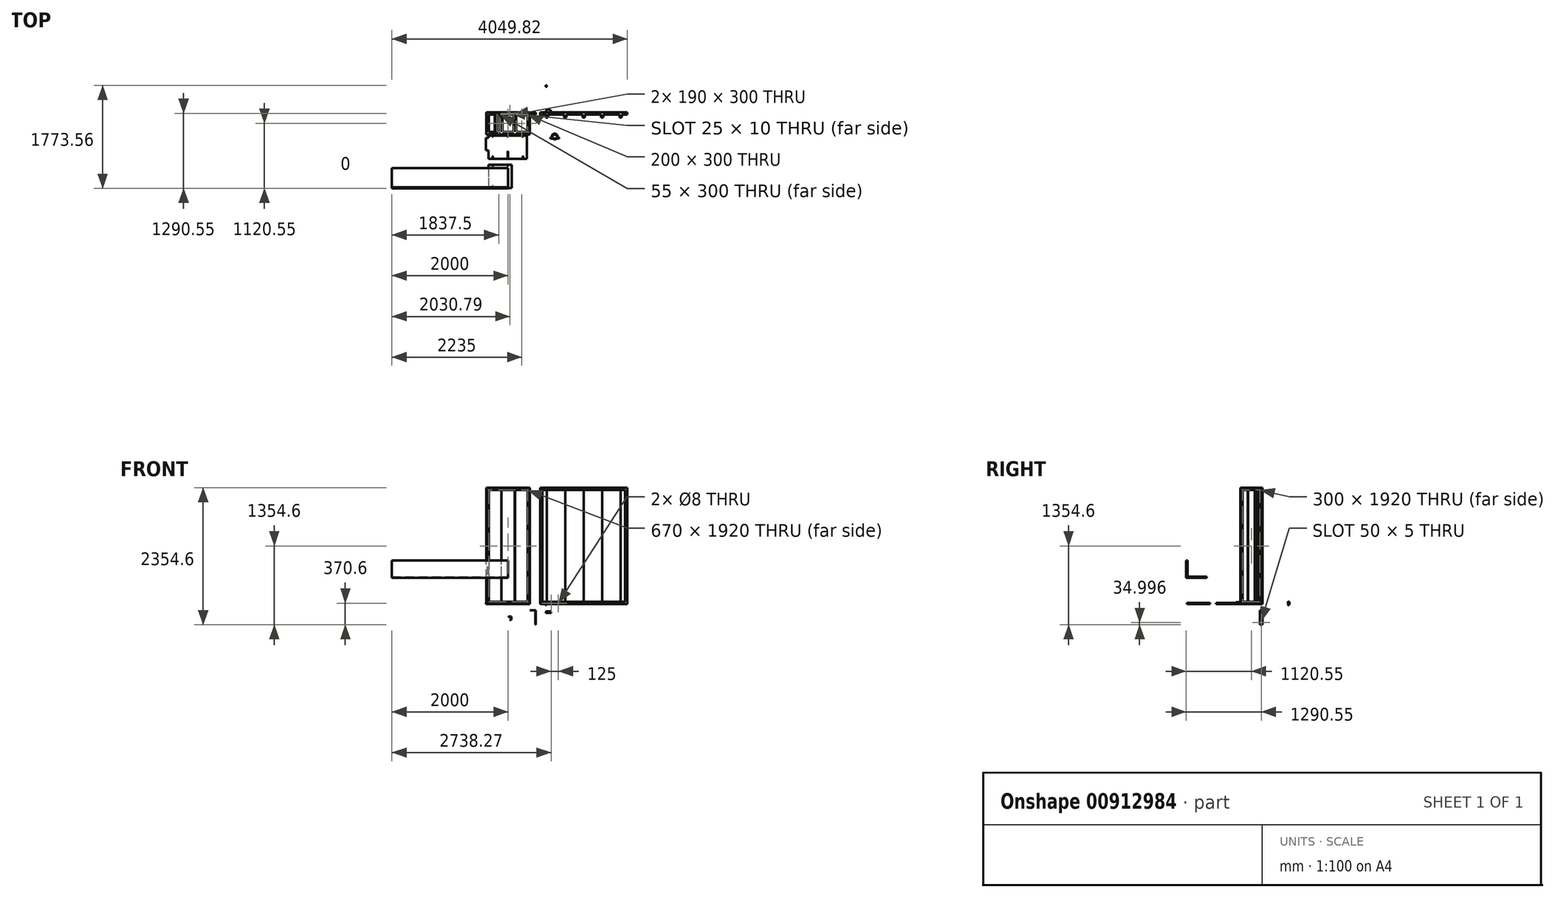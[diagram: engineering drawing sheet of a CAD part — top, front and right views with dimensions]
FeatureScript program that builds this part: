
annotation { "Feature Type Name" : "Feature", "Feature Type Description" : "" }
export const myFeature = defineFeature(function(context is Context, id is Id, definition is map)
    precondition{}
    {
        {
            assignVariable(context, id + "F0", {"name" : "widthA", "anyValue" : 380});
        }
        {
            assignVariable(context, id + "F1", {"name" : "widthB", "anyValue" : 90});
        }
        {
            var Q0;
            Q0=qCreatedBy(makeId("Front.planeOp"),FACE);
            var sketch = newSketch(context, id + "F2", { "sketchPlane" : qUnion([Q0])});
            skLineSegment(sketch, "E0.bottom", {"start": v(0, 0) * mm, "end": v(-750, 0) * mm});
            skLineSegment(sketch, "E0.top", {"start": v(0, 2000) * mm, "end": v(-750, 2000) * mm});
            skLineSegment(sketch, "E0.left", {"start": v(0, 0) * mm, "end": v(0, 2000) * mm});
            skLineSegment(sketch, "E0.right", {"start": v(-750, 0) * mm, "end": v(-750, 2000) * mm});
            skSolve(sketch);
        }
        {
            var Q0;
            Q0 = qSketchRegion(id + "F2", true);
            extrude(context, id + "F3", {"entities" : qUnion([Q0]), "depth" : (getVariable(context, 'widthA')) * mm, "offsetDistance" : 25 * mm});
        }
        {
            var Q0;
            Q0=makeQuery(id+"F3.opExtrude","CAP_FACE",FACE,{"disambiguationData":[OSD([sQuery(id+"F2.wireOp",EDGE,"E0.bottom"),sQuery(id+"F2.wireOp",EDGE,"E0.top"),sQuery(id+"F2.wireOp",EDGE,"E0.left"),sQuery(id+"F2.wireOp",EDGE,"E0.right")])],"isStart":false});
            var sketch = newSketch(context, id + "F4", { "sketchPlane" : qUnion([Q0])});
            skLineSegment(sketch, "E1.bottom", {"start": v(-710, 1960) * mm, "end": v(-40, 1960) * mm});
            skLineSegment(sketch, "E1.top", {"start": v(-710, 40) * mm, "end": v(-40, 40) * mm});
            skLineSegment(sketch, "E1.left", {"start": v(-710, 1960) * mm, "end": v(-710, 40) * mm});
            skLineSegment(sketch, "E1.right", {"start": v(-40, 1960) * mm, "end": v(-40, 40) * mm});
            skSolve(sketch);
        }
        {
            var Q0;
            Q0 = qSketchRegion(id + "F4", true);
            extrude(context, id + "F5", {"entities" : qUnion([Q0]), "operationType" : NewBodyOperationType.REMOVE, "endBound" : BoundingType.UP_TO_NEXT, "oppositeDirection" : true, "depth" : 25 * mm, "offsetDistance" : 25 * mm});
        }
        {
            var Q0;
            Q0=makeQuery(id+"F3.opExtrude","SWEPT_FACE",FACE,{"disambiguationData":[OSD([sQuery(id+"F2.wireOp",EDGE,"E0.right")])]});
            var sketch = newSketch(context, id + "F6", { "sketchPlane" : qUnion([Q0])});
            skLineSegment(sketch, "E2.bottom", {"start": v(40, 1960) * mm, "end": v(340, 1960) * mm});
            skLineSegment(sketch, "E2.top", {"start": v(40, 40) * mm, "end": v(340, 40) * mm});
            skLineSegment(sketch, "E2.left", {"start": v(40, 1960) * mm, "end": v(40, 40) * mm});
            skLineSegment(sketch, "E2.right", {"start": v(340, 1960) * mm, "end": v(340, 40) * mm});
            skSolve(sketch);
        }
        {
            var Q0;
            Q0 = qSketchRegion(id + "F6", true);
            var Q1;
            Q1=makeQuery(id+"F3.opExtrude","SWEPT_FACE",FACE,{"disambiguationData":[OSD([sQuery(id+"F2.wireOp",EDGE,"E0.left")])]});
            extrude(context, id + "F7", {"entities" : qUnion([Q0]), "operationType" : NewBodyOperationType.REMOVE, "endBound" : BoundingType.UP_TO_SURFACE, "oppositeDirection" : true, "depth" : 25 * mm, "endBoundEntityFace" : qUnion([Q1]), "offsetDistance" : 25 * mm});
        }
        {
            var Q0;
            Q0=makeQuery(id+"F3.opExtrude","SWEPT_FACE",FACE,{"disambiguationData":[OSD([sQuery(id+"F2.wireOp",EDGE,"E0.bottom")])]});
            var sketch = newSketch(context, id + "F8", { "sketchPlane" : qUnion([Q0])});
            skLineSegment(sketch, "E3.bottom", {"start": v(-40, 40) * mm, "end": v(-710, 40) * mm});
            skLineSegment(sketch, "E3.top", {"start": v(-40, 340) * mm, "end": v(-710, 340) * mm});
            skLineSegment(sketch, "E3.left", {"start": v(-40, 40) * mm, "end": v(-40, 340) * mm});
            skLineSegment(sketch, "E3.right", {"start": v(-710, 40) * mm, "end": v(-710, 340) * mm});
            skSolve(sketch);
        }
        {
            var Q0;
            Q0 = qSketchRegion(id + "F8", true);
            var Q1;
            Q1=makeQuery(id+"F3.opExtrude","SWEPT_FACE",FACE,{"disambiguationData":[OSD([sQuery(id+"F2.wireOp",EDGE,"E0.top")])]});
            extrude(context, id + "F9", {"entities" : qUnion([Q0]), "operationType" : NewBodyOperationType.REMOVE, "endBound" : BoundingType.UP_TO_SURFACE, "oppositeDirection" : true, "depth" : 25 * mm, "endBoundEntityFace" : qUnion([Q1]), "offsetDistance" : 25 * mm});
        }
        {
            var Q0;
            Q0=makeQuery(id+"F9.boolean.opBoolean","COPY",FACE,{"disambiguationData":[TD([makeQuery(id+"F3.opExtrude","SWEPT_FACE",FACE,{"disambiguationData":[OSD([sQuery(id+"F2.wireOp",EDGE,"E0.top")])]})])],"derivedFrom":makeQuery(id+"F9.opExtrude","SWEPT_FACE",FACE,{"disambiguationData":[OSD([sQuery(id+"F8.wireOp",EDGE,"E3.bottom")])]})});
            var sketch = newSketch(context, id + "F10", { "sketchPlane" : qUnion([Q0])});
            skLineSegment(sketch, "E4.bottom", {"start": v(-510, 2000) * mm, "end": v(-470, 2000) * mm});
            skLineSegment(sketch, "E4.top", {"start": v(-510, 1960) * mm, "end": v(-470, 1960) * mm});
            skLineSegment(sketch, "E4.left", {"start": v(-510, 2000) * mm, "end": v(-510, 1960) * mm});
            skLineSegment(sketch, "E4.right", {"start": v(-470, 2000) * mm, "end": v(-470, 1960) * mm});
            skLineSegment(sketch, "E5", {"start": v(-375, 2000) * mm, "end": v(-375, 1960) * mm, "construction": true});
            skLineSegment(sketch, "E6.MirrorCS", {"start": v(-240, 2000) * mm, "end": v(-280, 2000) * mm});
            skLineSegment(sketch, "E7.MirrorCS", {"start": v(-240, 2000) * mm, "end": v(-240, 1960) * mm});
            skLineSegment(sketch, "E8.MirrorCS", {"start": v(-240, 1960) * mm, "end": v(-280, 1960) * mm});
            skLineSegment(sketch, "E9.MirrorCS", {"start": v(-280, 2000) * mm, "end": v(-280, 1960) * mm});
            skLineSegment(sketch, "E10", {"start": v(-710, 1000) * mm, "end": v(-43.6, 1000) * mm, "construction": true});
            skLineSegment(sketch, "E11.MirrorCS", {"start": v(-510, 0) * mm, "end": v(-510, 40) * mm});
            skLineSegment(sketch, "E12.MirrorCS", {"start": v(-470, 0) * mm, "end": v(-470, 40) * mm});
            skLineSegment(sketch, "E13.MirrorCS", {"start": v(-510, 40) * mm, "end": v(-470, 40) * mm});
            skLineSegment(sketch, "E14.MirrorCS", {"start": v(-510, 0) * mm, "end": v(-470, 0) * mm});
            skLineSegment(sketch, "E15.MirrorCS", {"start": v(-240, 40) * mm, "end": v(-280, 40) * mm});
            skLineSegment(sketch, "E16.MirrorCS", {"start": v(-280, 0) * mm, "end": v(-280, 40) * mm});
            skLineSegment(sketch, "E17.MirrorCS", {"start": v(-240, 0) * mm, "end": v(-240, 40) * mm});
            skLineSegment(sketch, "E18.MirrorCS", {"start": v(-240, 0) * mm, "end": v(-280, 0) * mm});
            skSolve(sketch);
        }
        {
            var Q0;
            Q0 = qSketchRegion(id + "F10", true);
            extrude(context, id + "F11", {"entities" : qUnion([Q0]), "operationType" : NewBodyOperationType.ADD, "endBound" : BoundingType.UP_TO_NEXT, "depth" : 25 * mm, "offsetDistance" : 25 * mm});
        }
        {
            var Q0;
            Q0=makeQuery(id+"F3.opExtrude","CAP_FACE",FACE,{"disambiguationData":[OSD([sQuery(id+"F2.wireOp",EDGE,"E0.bottom"),sQuery(id+"F2.wireOp",EDGE,"E0.top"),sQuery(id+"F2.wireOp",EDGE,"E0.left"),sQuery(id+"F2.wireOp",EDGE,"E0.right")])],"isStart":false});
            var Q1;
            Q1=makeQuery(id+"F3.opExtrude","CAP_FACE",FACE,{"disambiguationData":[OSD([sQuery(id+"F2.wireOp",EDGE,"E0.bottom"),sQuery(id+"F2.wireOp",EDGE,"E0.top"),sQuery(id+"F2.wireOp",EDGE,"E0.left"),sQuery(id+"F2.wireOp",EDGE,"E0.right")])],"isStart":true});
            cPlane(context, id + "F12", {"entities" : qUnion([Q0, Q1]), "cplaneType" : CPlaneType.MID_PLANE, "offset" : 25 * mm, "width" : 150 * mm, "height" : 150 * mm});
        }
        {
            var Q0;
            Q0=makeQuery(id+"F3.opExtrude","SWEPT_FACE",FACE,{"disambiguationData":[OSD([sQuery(id+"F2.wireOp",EDGE,"E0.right")])]});
            var Q1;
            Q1=makeQuery(id+"F3.opExtrude","SWEPT_FACE",FACE,{"disambiguationData":[OSD([sQuery(id+"F2.wireOp",EDGE,"E0.left")])]});
            cPlane(context, id + "F13", {"entities" : qUnion([Q0, Q1]), "cplaneType" : CPlaneType.MID_PLANE, "offset" : 25 * mm, "width" : 150 * mm, "height" : 150 * mm});
        }
        {
            var Q0;
            {var subQ1=makeQuery(id+"F5.boolean.opBoolean","COPY",FACE,{"derivedFrom":makeQuery(id+"F5.opExtrude","SWEPT_FACE",FACE,{"disambiguationData":[OSD([sQuery(id+"F4.wireOp",EDGE,"E1.bottom")])]})});var subQ3=sQuery(id+"F2.wireOp",EDGE,"E0.right");var subQ4=sQuery(id+"F2.wireOp",EDGE,"E0.left");var subQ6=makeQuery(id+"F7.opExtrude","SWEPT_FACE",FACE,{"disambiguationData":[OSD([sQuery(id+"F6.wireOp",EDGE,"E2.bottom")])]});Q0=makeQuery(id+"F9.boolean.opBoolean","SPLIT",FACE,{"disambiguationData":[TD([makeQuery(id+"F3.opExtrude","CAP_FACE",FACE,{"disambiguationData":[OSD([sQuery(id+"F2.wireOp",EDGE,"E0.bottom"),sQuery(id+"F2.wireOp",EDGE,"E0.top"),subQ4,subQ3])],"isStart":false})])],"derivedFrom":makeQuery(id+"F7.boolean.opBoolean","MERGE",FACE,{"derivedFrom":[subQ1],"fromTools":[subQ6]})});}
            cPlane(context, id + "F14", {"entities" : qUnion([Q0]), "cplaneType" : CPlaneType.OFFSET, "offset" : 0 * mm, "width" : 150 * mm, "height" : 150 * mm});
        }
        {
            var Q0;
            Q0=qCreatedBy(id+"F14.planeOp",FACE);
            var sketch = newSketch(context, id + "F15", { "sketchPlane" : qUnion([Q0])});
            skCircle(sketch, "E19", {"center": v(-490, 250) * mm, "radius": 2 * mm});
            skCircle(sketch, "E20.MirrorC", {"center": v(-260, 250) * mm, "radius": 2 * mm});
            skCircle(sketch, "E21.MirrorC", {"center": v(-490, 130) * mm, "radius": 2 * mm});
            skCircle(sketch, "E22.MirrorC", {"center": v(-260, 130) * mm, "radius": 2 * mm});
            skCircle(sketch, "E23", {"center": v(-730, 250) * mm, "radius": 2 * mm});
            skLineSegment(sketch, "E24", {"start": v(-750.33, 190) * mm, "end": v(0, 190) * mm, "construction": true});
            skLineSegment(sketch, "E25", {"start": v(-375, 299.5) * mm, "end": v(-375, 0) * mm, "construction": true});
            skCircle(sketch, "E26.MirrorC", {"center": v(-20, 250) * mm, "radius": 2 * mm});
            skCircle(sketch, "E27.MirrorC", {"center": v(-730, 130) * mm, "radius": 2 * mm});
            skCircle(sketch, "E28.MirrorC", {"center": v(-20, 130) * mm, "radius": 2 * mm});
            skSolve(sketch);
        }
        {
            var Q0;
            Q0 = qSketchRegion(id + "F15", true);
            extrude(context, id + "F16", {"entities" : qUnion([Q0]), "operationType" : NewBodyOperationType.ADD, "endBound" : BoundingType.UP_TO_NEXT, "depth" : 25 * mm, "offsetDistance" : 25 * mm});
        }
        {
            var Q0;
            Q0=qCreatedBy(makeId("Front.planeOp"),FACE);
            var sketch = newSketch(context, id + "F17", { "sketchPlane" : qUnion([Q0])});
            skLineSegment(sketch, "E29.bottom", {"start": v(174.82, 0) * mm, "end": v(1674.82, 0) * mm});
            skLineSegment(sketch, "E29.top", {"start": v(174.82, 2000) * mm, "end": v(1674.82, 2000) * mm});
            skLineSegment(sketch, "E29.left", {"start": v(174.82, 0) * mm, "end": v(174.82, 2000) * mm});
            skLineSegment(sketch, "E29.right", {"start": v(1674.82, 0) * mm, "end": v(1674.82, 2000) * mm});
            skSolve(sketch);
        }
        {
            var Q0;
            Q0 = qSketchRegion(id + "F17", true);
            extrude(context, id + "F18", {"entities" : qUnion([Q0]), "depth" : 40 * mm, "offsetDistance" : 25 * mm});
        }
        {
            var Q0;
            Q0=makeQuery(id+"F18.opExtrude","CAP_FACE",FACE,{"disambiguationData":[OSD([sQuery(id+"F17.wireOp",EDGE,"E29.bottom"),sQuery(id+"F17.wireOp",EDGE,"E29.top"),sQuery(id+"F17.wireOp",EDGE,"E29.left"),sQuery(id+"F17.wireOp",EDGE,"E29.right")])],"isStart":false});
            var sketch = newSketch(context, id + "F19", { "sketchPlane" : qUnion([Q0])});
            skLineSegment(sketch, "E30.bottom", {"start": v(214.82, 1960) * mm, "end": v(1634.82, 1960) * mm});
            skLineSegment(sketch, "E30.top", {"start": v(214.82, 40) * mm, "end": v(1634.82, 40) * mm});
            skLineSegment(sketch, "E30.left", {"start": v(214.82, 1960) * mm, "end": v(214.82, 40) * mm});
            skLineSegment(sketch, "E30.right", {"start": v(1634.82, 1960) * mm, "end": v(1634.82, 40) * mm});
            skSolve(sketch);
        }
        {
            var Q0;
            Q0 = qSketchRegion(id + "F19", true);
            extrude(context, id + "F20", {"entities" : qUnion([Q0]), "operationType" : NewBodyOperationType.REMOVE, "endBound" : BoundingType.UP_TO_NEXT, "oppositeDirection" : true, "depth" : 25 * mm, "offsetDistance" : 25 * mm});
        }
        {
            var Q0;
            Q0=makeQuery(id+"F18.opExtrude","SWEPT_FACE",FACE,{"disambiguationData":[OSD([sQuery(id+"F17.wireOp",EDGE,"E29.right")])]});
            var Q1;
            Q1=makeQuery(id+"F18.opExtrude","SWEPT_FACE",FACE,{"disambiguationData":[OSD([sQuery(id+"F17.wireOp",EDGE,"E29.left")])]});
            cPlane(context, id + "F21", {"entities" : qUnion([Q0, Q1]), "cplaneType" : CPlaneType.MID_PLANE, "offset" : 25 * mm, "width" : 150 * mm, "height" : 150 * mm});
        }
        {
            var Q0;
            Q0=makeQuery(id+"F18.opExtrude","SWEPT_FACE",FACE,{"disambiguationData":[OSD([sQuery(id+"F17.wireOp",EDGE,"E29.top")])]});
            var Q1;
            Q1=makeQuery(id+"F18.opExtrude","SWEPT_FACE",FACE,{"disambiguationData":[OSD([sQuery(id+"F17.wireOp",EDGE,"E29.bottom")])]});
            cPlane(context, id + "F22", {"entities" : qUnion([Q0, Q1]), "cplaneType" : CPlaneType.MID_PLANE, "offset" : 25 * mm, "width" : 150 * mm, "height" : 150 * mm});
        }
        {
            var Q0;
            Q0=makeQuery(id+"F18.opExtrude","CAP_FACE",FACE,{"disambiguationData":[OSD([sQuery(id+"F17.wireOp",EDGE,"E29.bottom"),sQuery(id+"F17.wireOp",EDGE,"E29.top"),sQuery(id+"F17.wireOp",EDGE,"E29.left"),sQuery(id+"F17.wireOp",EDGE,"E29.right")])],"isStart":false});
            var sketch = newSketch(context, id + "F23", { "sketchPlane" : qUnion([Q0])});
            skLineSegment(sketch, "E31.bottom", {"start": v(269.82, 2000) * mm, "end": v(309.82, 2000) * mm});
            skLineSegment(sketch, "E31.top", {"start": v(269.82, 1960) * mm, "end": v(309.82, 1960) * mm});
            skLineSegment(sketch, "E31.left", {"start": v(269.82, 2000) * mm, "end": v(269.82, 1960) * mm});
            skLineSegment(sketch, "E31.right", {"start": v(309.82, 2000) * mm, "end": v(309.82, 1960) * mm});
            skLineSegment(sketch, "E32.bottom", {"start": v(587.32, 2000) * mm, "end": v(627.32, 2000) * mm});
            skLineSegment(sketch, "E32.top", {"start": v(587.32, 1960) * mm, "end": v(627.32, 1960) * mm});
            skLineSegment(sketch, "E32.left", {"start": v(587.32, 2000) * mm, "end": v(587.32, 1960) * mm});
            skLineSegment(sketch, "E32.right", {"start": v(627.32, 2000) * mm, "end": v(627.32, 1960) * mm});
            skLineSegment(sketch, "E33.bottom", {"start": v(904.82, 2000) * mm, "end": v(944.82, 2000) * mm});
            skLineSegment(sketch, "E33.top", {"start": v(904.82, 1960) * mm, "end": v(944.82, 1960) * mm});
            skLineSegment(sketch, "E33.left", {"start": v(904.82, 2000) * mm, "end": v(904.82, 1960) * mm});
            skLineSegment(sketch, "E33.right", {"start": v(944.82, 2000) * mm, "end": v(944.82, 1960) * mm});
            skPoint(sketch, "E34", {"position": v(924.82, 2000) * mm});
            skPoint(sketch, "E35", {"position": v(607.32, 2000) * mm});
            skPoint(sketch, "E36", {"position": v(289.82, 2000) * mm});
            skLineSegment(sketch, "E37", {"start": v(289.82, 2000) * mm, "end": v(924.82, 2000) * mm, "construction": true});
            skLineSegment(sketch, "E38.MirrorCS", {"start": v(1262.32, 2000) * mm, "end": v(1222.32, 2000) * mm});
            skLineSegment(sketch, "E39.MirrorCS", {"start": v(1222.32, 2000) * mm, "end": v(1222.32, 1960) * mm});
            skLineSegment(sketch, "E40.MirrorCS", {"start": v(1262.32, 1960) * mm, "end": v(1222.32, 1960) * mm});
            skLineSegment(sketch, "E41.MirrorCS", {"start": v(1262.32, 2000) * mm, "end": v(1262.32, 1960) * mm});
            skLineSegment(sketch, "E42.MirrorCS", {"start": v(1579.82, 1960) * mm, "end": v(1539.82, 1960) * mm});
            skLineSegment(sketch, "E43.MirrorCS", {"start": v(1539.82, 2000) * mm, "end": v(1539.82, 1960) * mm});
            skLineSegment(sketch, "E44.MirrorCS", {"start": v(1579.82, 2000) * mm, "end": v(1579.82, 1960) * mm});
            skLineSegment(sketch, "E45.MirrorCS", {"start": v(1579.82, 2000) * mm, "end": v(1539.82, 2000) * mm});
            skLineSegment(sketch, "E46.MirrorCS", {"start": v(587.32, 0) * mm, "end": v(627.32, 0) * mm});
            skLineSegment(sketch, "E47.MirrorCS", {"start": v(587.32, 0) * mm, "end": v(587.32, 40) * mm});
            skLineSegment(sketch, "E48.MirrorCS", {"start": v(904.82, 0) * mm, "end": v(904.82, 40) * mm});
            skLineSegment(sketch, "E49.MirrorCS", {"start": v(269.82, 0) * mm, "end": v(269.82, 40) * mm});
            skLineSegment(sketch, "E50.MirrorCS", {"start": v(904.82, 0) * mm, "end": v(944.82, 0) * mm});
            skLineSegment(sketch, "E51.MirrorCS", {"start": v(269.82, 0) * mm, "end": v(309.82, 0) * mm});
            skLineSegment(sketch, "E52.MirrorCS", {"start": v(1579.82, 40) * mm, "end": v(1539.82, 40) * mm});
            skLineSegment(sketch, "E53.MirrorCS", {"start": v(1262.32, 0) * mm, "end": v(1262.32, 40) * mm});
            skLineSegment(sketch, "E54.MirrorCS", {"start": v(1222.32, 0) * mm, "end": v(1222.32, 40) * mm});
            skLineSegment(sketch, "E55.MirrorCS", {"start": v(1579.82, 0) * mm, "end": v(1539.82, 0) * mm});
            skLineSegment(sketch, "E56.MirrorCS", {"start": v(269.82, 40) * mm, "end": v(309.82, 40) * mm});
            skLineSegment(sketch, "E57.MirrorCS", {"start": v(587.32, 40) * mm, "end": v(627.32, 40) * mm});
            skLineSegment(sketch, "E58.MirrorCS", {"start": v(1262.32, 40) * mm, "end": v(1222.32, 40) * mm});
            skLineSegment(sketch, "E59.MirrorCS", {"start": v(1262.32, 0) * mm, "end": v(1222.32, 0) * mm});
            skLineSegment(sketch, "E60.MirrorCS", {"start": v(944.82, 0) * mm, "end": v(944.82, 40) * mm});
            skLineSegment(sketch, "E61.MirrorCS", {"start": v(627.32, 0) * mm, "end": v(627.32, 40) * mm});
            skLineSegment(sketch, "E62.MirrorCS", {"start": v(309.82, 0) * mm, "end": v(309.82, 40) * mm});
            skLineSegment(sketch, "E63.MirrorCS", {"start": v(1579.82, 0) * mm, "end": v(1579.82, 40) * mm});
            skLineSegment(sketch, "E64.MirrorCS", {"start": v(1539.82, 0) * mm, "end": v(1539.82, 40) * mm});
            skLineSegment(sketch, "E65.MirrorCS", {"start": v(904.82, 40) * mm, "end": v(944.82, 40) * mm});
            skPoint(sketch, "E66.MirrorP", {"position": v(607.32, 0) * mm});
            skPoint(sketch, "E67.MirrorP", {"position": v(289.82, 0) * mm});
            skPoint(sketch, "E68.MirrorP", {"position": v(924.82, 0) * mm});
            skLineSegment(sketch, "E69.MirrorCS", {"start": v(289.82, 0) * mm, "end": v(924.82, 0) * mm, "construction": true});
            skLineSegment(sketch, "E70.bottom", {"start": v(214.82, 1960) * mm, "end": v(174.82, 1960) * mm});
            skLineSegment(sketch, "E70.top", {"start": v(214.82, 2000) * mm, "end": v(174.82, 2000) * mm});
            skLineSegment(sketch, "E70.left", {"start": v(214.82, 1960) * mm, "end": v(214.82, 2000) * mm});
            skLineSegment(sketch, "E70.right", {"start": v(174.82, 1960) * mm, "end": v(174.82, 2000) * mm});
            skLineSegment(sketch, "E71.bottom", {"start": v(214.82, 40) * mm, "end": v(174.82, 40) * mm});
            skLineSegment(sketch, "E71.top", {"start": v(214.82, 0) * mm, "end": v(174.82, 0) * mm});
            skLineSegment(sketch, "E71.left", {"start": v(214.82, 40) * mm, "end": v(214.82, 0) * mm});
            skLineSegment(sketch, "E71.right", {"start": v(174.82, 40) * mm, "end": v(174.82, 0) * mm});
            skSolve(sketch);
        }
        {
            var Q0;
            Q0 = qSketchRegion(id + "F23", true);
            extrude(context, id + "F24", {"entities" : qUnion([Q0]), "operationType" : NewBodyOperationType.ADD, "depth" : (getVariable(context, 'widthB') - 40) * mm, "offsetDistance" : 25 * mm});
        }
        {
            var Q0;
            Q0=makeQuery(id+"F24.opExtrude","SWEPT_FACE",FACE,{"disambiguationData":[OSD([sQuery(id+"F23.wireOp",EDGE,"E31.right")])]});
            var Q1;
            Q1=makeQuery(id+"F24.opExtrude","SWEPT_FACE",FACE,{"disambiguationData":[OSD([sQuery(id+"F23.wireOp",EDGE,"E31.left")])]});
            cPlane(context, id + "F25", {"entities" : qUnion([Q0, Q1]), "cplaneType" : CPlaneType.MID_PLANE, "offset" : 25 * mm, "width" : 150 * mm, "height" : 150 * mm});
        }
        {
            var Q0;
            Q0=makeQuery(id+"F24.boolean.opBoolean","MERGE",FACE,{"derivedFrom":[makeQuery(id+"F20.boolean.opBoolean","COPY",FACE,{"derivedFrom":makeQuery(id+"F20.opExtrude","SWEPT_FACE",FACE,{"disambiguationData":[OSD([sQuery(id+"F19.wireOp",EDGE,"E30.bottom")])]})}),makeQuery(id+"F24.opExtrude","SWEPT_FACE",FACE,{"disambiguationData":[OSD([sQuery(id+"F23.wireOp",EDGE,"E31.top")])]}),makeQuery(id+"F24.opExtrude","SWEPT_FACE",FACE,{"disambiguationData":[OSD([sQuery(id+"F23.wireOp",EDGE,"E32.top")])]}),makeQuery(id+"F24.opExtrude","SWEPT_FACE",FACE,{"disambiguationData":[OSD([sQuery(id+"F23.wireOp",EDGE,"E33.top")])]}),makeQuery(id+"F24.opExtrude","SWEPT_FACE",FACE,{"disambiguationData":[OSD([sQuery(id+"F23.wireOp",EDGE,"E40.MirrorCS")])]}),makeQuery(id+"F24.opExtrude","SWEPT_FACE",FACE,{"disambiguationData":[OSD([sQuery(id+"F23.wireOp",EDGE,"E42.MirrorCS")])]})]});
            var sketch = newSketch(context, id + "F26", { "sketchPlane" : qUnion([Q0])});
            skCircle(sketch, "E72", {"center": v(289.82, 10) * mm, "radius": 2 * mm});
            skCircle(sketch, "E73", {"center": v(289.82, 80) * mm, "radius": 2 * mm});
            skCircle(sketch, "E74.1.0.0", {"center": v(607.32, 80) * mm, "radius": 2 * mm});
            skCircle(sketch, "E74.1.0.1", {"center": v(607.32, 10) * mm, "radius": 2 * mm});
            skCircle(sketch, "E74.2.0.0", {"center": v(924.82, 80) * mm, "radius": 2 * mm});
            skCircle(sketch, "E74.2.0.1", {"center": v(924.82, 10) * mm, "radius": 2 * mm});
            skCircle(sketch, "E74.3.0.0", {"center": v(1242.32, 80) * mm, "radius": 2 * mm});
            skCircle(sketch, "E74.3.0.1", {"center": v(1242.32, 10) * mm, "radius": 2 * mm});
            skCircle(sketch, "E74.4.0.0", {"center": v(1559.82, 80) * mm, "radius": 2 * mm});
            skCircle(sketch, "E74.4.0.1", {"center": v(1559.82, 10) * mm, "radius": 2 * mm});
            skLineSegment(sketch, "E74.direction1", {"start": v(289.82, 80) * mm, "end": v(607.32, 80) * mm, "construction": true});
            skSolve(sketch);
        }
        {
            var Q0;
            Q0 = qSketchRegion(id + "F26", true);
            extrude(context, id + "F27", {"entities" : qUnion([Q0]), "operationType" : NewBodyOperationType.ADD, "endBound" : BoundingType.UP_TO_NEXT, "depth" : 25 * mm, "offsetDistance" : 25 * mm});
        }
        {
            var Q0;
            Q0=qCreatedBy(makeId("Top.planeOp"),FACE);
            var sketch = newSketch(context, id + "F28", { "sketchPlane" : qUnion([Q0])});
            skLineSegment(sketch, "E75.bottom", {"start": v(-711.31, -400.12) * mm, "end": v(-643.81, -400.12) * mm});
            skLineSegment(sketch, "E75.top", {"start": v(-711.31, -800.12) * mm, "end": v(-643.81, -800.12) * mm});
            skLineSegment(sketch, "E75.left", {"start": v(-711.31, -400.12) * mm, "end": v(-711.31, -800.12) * mm});
            skLineSegment(sketch, "E75.right", {"start": v(-51.31, -400.12) * mm, "end": v(-51.31, -800.12) * mm});
            skLineSegment(sketch, "E76", {"start": v(-381.31, -400.12) * mm, "end": v(-381.31, -800.12) * mm, "construction": true});
            skLineSegment(sketch, "E77.top", {"start": v(-381.31, -422.62) * mm, "end": v(-381.31, -422.62) * mm});
            skLineSegment(sketch, "E77.left", {"start": v(-378.81, -400.12) * mm, "end": v(-378.81, -420.12) * mm});
            skLineSegment(sketch, "E77.right", {"start": v(-383.81, -400.12) * mm, "end": v(-383.81, -420.12) * mm});
            skLineSegment(sketch, "E78.top", {"start": v(-381.31, -677.62) * mm, "end": v(-381.31, -677.62) * mm});
            skLineSegment(sketch, "E78.left", {"start": v(-378.81, -800.12) * mm, "end": v(-378.81, -680.12) * mm});
            skLineSegment(sketch, "E78.right", {"start": v(-383.81, -800.12) * mm, "end": v(-383.81, -680.12) * mm});
            skLineSegment(sketch, "E79.top", {"start": v(-641.31, -757.62) * mm, "end": v(-641.31, -757.62) * mm});
            skLineSegment(sketch, "E79.left", {"start": v(-638.81, -800.12) * mm, "end": v(-638.81, -760.12) * mm});
            skLineSegment(sketch, "E79.right", {"start": v(-643.81, -800.12) * mm, "end": v(-643.81, -760.12) * mm});
            skLineSegment(sketch, "E80.top", {"start": v(-641.31, -422.62) * mm, "end": v(-641.31, -422.62) * mm});
            skLineSegment(sketch, "E80.left", {"start": v(-638.81, -400.12) * mm, "end": v(-638.81, -420.12) * mm});
            skLineSegment(sketch, "E80.right", {"start": v(-643.81, -400.12) * mm, "end": v(-643.81, -420.12) * mm});
            skLineSegment(sketch, "E81.trimOffspring", {"start": v(-638.81, -800.12) * mm, "end": v(-383.81, -800.12) * mm});
            skLineSegment(sketch, "E82.trimOffspring", {"start": v(-378.81, -800.12) * mm, "end": v(-123.81, -800.12) * mm});
            skLineSegment(sketch, "E83.trimOffspring", {"start": v(-378.81, -400.12) * mm, "end": v(-123.81, -400.12) * mm});
            skLineSegment(sketch, "E84.trimOffspring", {"start": v(-638.81, -400.12) * mm, "end": v(-383.81, -400.12) * mm});
            skPoint(sketch, "E85", {"position": v(-381.31, -677.62) * mm});
            skPoint(sketch, "E86", {"position": v(-381.31, -422.62) * mm});
            skLineSegment(sketch, "E87", {"start": v(-641.31, -385.2) * mm, "end": v(-641.31, -738.61) * mm, "construction": true});
            skPoint(sketch, "E88", {"position": v(-641.31, -757.62) * mm});
            skPoint(sketch, "E89", {"position": v(-641.31, -422.62) * mm});
            skPoint(sketch, "E90.visualSharp", {"position": v(-643.81, -422.62) * mm});
            skArc(sketch, "E90.filletArc", {"start": v(-643.81, -420.12) * mm, "mid": v(-643.08, -421.88) * mm, "end": v(-641.31, -422.62) * mm});
            skPoint(sketch, "E91.visualSharp", {"position": v(-638.81, -422.62) * mm});
            skArc(sketch, "E91.filletArc", {"start": v(-641.31, -422.62) * mm, "mid": v(-639.55, -421.88) * mm, "end": v(-638.81, -420.12) * mm});
            skPoint(sketch, "E92.visualSharp", {"position": v(-383.81, -422.62) * mm});
            skArc(sketch, "E92.filletArc", {"start": v(-383.81, -420.12) * mm, "mid": v(-383.08, -421.88) * mm, "end": v(-381.31, -422.62) * mm});
            skPoint(sketch, "E93.visualSharp", {"position": v(-378.81, -422.62) * mm});
            skArc(sketch, "E93.filletArc", {"start": v(-381.31, -422.62) * mm, "mid": v(-379.55, -421.88) * mm, "end": v(-378.81, -420.12) * mm});
            skPoint(sketch, "E94.visualSharp", {"position": v(-383.81, -677.62) * mm});
            skArc(sketch, "E94.filletArc", {"start": v(-381.31, -677.62) * mm, "mid": v(-383.08, -678.35) * mm, "end": v(-383.81, -680.12) * mm});
            skPoint(sketch, "E95.visualSharp", {"position": v(-378.81, -677.62) * mm});
            skArc(sketch, "E95.filletArc", {"start": v(-378.81, -680.12) * mm, "mid": v(-379.55, -678.35) * mm, "end": v(-381.31, -677.62) * mm});
            skPoint(sketch, "E96.visualSharp", {"position": v(-643.81, -757.62) * mm});
            skArc(sketch, "E96.filletArc", {"start": v(-641.31, -757.62) * mm, "mid": v(-643.08, -758.35) * mm, "end": v(-643.81, -760.12) * mm});
            skPoint(sketch, "E97.visualSharp", {"position": v(-638.81, -757.62) * mm});
            skArc(sketch, "E97.filletArc", {"start": v(-638.81, -760.12) * mm, "mid": v(-639.55, -758.35) * mm, "end": v(-641.31, -757.62) * mm});
            skArc(sketch, "E98.MirrorCS", {"start": v(-118.81, -420.12) * mm, "mid": v(-119.55, -421.88) * mm, "end": v(-121.31, -422.62) * mm});
            skArc(sketch, "E99.MirrorCS", {"start": v(-121.31, -422.62) * mm, "mid": v(-123.08, -421.88) * mm, "end": v(-123.81, -420.12) * mm});
            skPoint(sketch, "E100.MirrorP", {"position": v(-121.31, -422.62) * mm});
            skPoint(sketch, "E101.MirrorP", {"position": v(-118.81, -422.62) * mm});
            skPoint(sketch, "E102.MirrorP", {"position": v(-123.81, -422.62) * mm});
            skLineSegment(sketch, "E103.MirrorCS", {"start": v(-121.31, -422.62) * mm, "end": v(-121.31, -422.62) * mm});
            skLineSegment(sketch, "E104.MirrorCS", {"start": v(-118.81, -400.12) * mm, "end": v(-118.81, -420.12) * mm});
            skLineSegment(sketch, "E105.MirrorCS", {"start": v(-123.81, -400.12) * mm, "end": v(-123.81, -420.12) * mm});
            skArc(sketch, "E106.MirrorCS", {"start": v(-121.31, -757.62) * mm, "mid": v(-119.55, -758.35) * mm, "end": v(-118.81, -760.12) * mm});
            skArc(sketch, "E107.MirrorCS", {"start": v(-123.81, -760.12) * mm, "mid": v(-123.08, -758.35) * mm, "end": v(-121.31, -757.62) * mm});
            skPoint(sketch, "E108.MirrorP", {"position": v(-121.31, -757.62) * mm});
            skPoint(sketch, "E109.MirrorP", {"position": v(-118.81, -757.62) * mm});
            skPoint(sketch, "E110.MirrorP", {"position": v(-123.81, -757.62) * mm});
            skLineSegment(sketch, "E111.MirrorCS", {"start": v(-121.31, -757.62) * mm, "end": v(-121.31, -757.62) * mm});
            skLineSegment(sketch, "E112.MirrorCS", {"start": v(-51.31, -800.12) * mm, "end": v(-118.81, -800.12) * mm});
            skLineSegment(sketch, "E113.MirrorCS", {"start": v(-123.81, -800.12) * mm, "end": v(-378.81, -800.12) * mm});
            skLineSegment(sketch, "E114.MirrorCS", {"start": v(-123.81, -800.12) * mm, "end": v(-123.81, -760.12) * mm});
            skLineSegment(sketch, "E115.MirrorCS", {"start": v(-118.81, -800.12) * mm, "end": v(-118.81, -760.12) * mm});
            skLineSegment(sketch, "E116.MirrorCS", {"start": v(-121.31, -385.2) * mm, "end": v(-121.31, -738.61) * mm, "construction": true});
            skLineSegment(sketch, "E117.trimOffspring", {"start": v(-118.81, -400.12) * mm, "end": v(-51.31, -400.12) * mm});
            skLineSegment(sketch, "E118.trimOffspring", {"start": v(-118.81, -800.12) * mm, "end": v(-51.31, -800.12) * mm});
            skLineSegment(sketch, "E119.bottom", {"start": v(-711.31, -903.75) * mm, "end": v(-643.81, -903.75) * mm});
            skLineSegment(sketch, "E119.top", {"start": v(-711.31, -1303.75) * mm, "end": v(-643.81, -1303.75) * mm});
            skLineSegment(sketch, "E119.left", {"start": v(-711.31, -903.75) * mm, "end": v(-711.31, -1303.75) * mm});
            skLineSegment(sketch, "E119.right", {"start": v(-311.31, -903.75) * mm, "end": v(-311.31, -1303.75) * mm});
            skLineSegment(sketch, "E120.top", {"start": v(-641.31, -926.25) * mm, "end": v(-641.31, -926.25) * mm});
            skLineSegment(sketch, "E120.left", {"start": v(-643.81, -903.75) * mm, "end": v(-643.81, -923.75) * mm});
            skLineSegment(sketch, "E120.right", {"start": v(-638.81, -903.75) * mm, "end": v(-638.81, -923.75) * mm});
            skLineSegment(sketch, "E121.top", {"start": v(-381.31, -926.25) * mm, "end": v(-381.31, -926.25) * mm});
            skLineSegment(sketch, "E121.left", {"start": v(-383.81, -903.75) * mm, "end": v(-383.81, -923.75) * mm});
            skLineSegment(sketch, "E121.right", {"start": v(-378.81, -903.75) * mm, "end": v(-378.81, -923.75) * mm});
            skLineSegment(sketch, "E122.top", {"start": v(-641.31, -1261.25) * mm, "end": v(-641.31, -1261.25) * mm});
            skLineSegment(sketch, "E122.left", {"start": v(-643.81, -1303.75) * mm, "end": v(-643.81, -1263.75) * mm});
            skLineSegment(sketch, "E122.right", {"start": v(-638.81, -1303.75) * mm, "end": v(-638.81, -1263.75) * mm});
            skLineSegment(sketch, "E123.top", {"start": v(-381.31, -1261.25) * mm, "end": v(-381.31, -1261.25) * mm});
            skLineSegment(sketch, "E123.left", {"start": v(-383.81, -1303.75) * mm, "end": v(-383.81, -1263.75) * mm});
            skLineSegment(sketch, "E123.right", {"start": v(-378.81, -1303.75) * mm, "end": v(-378.81, -1263.75) * mm});
            skPoint(sketch, "E124.visualSharp", {"position": v(-643.81, -926.25) * mm});
            skArc(sketch, "E124.filletArc", {"start": v(-643.81, -923.75) * mm, "mid": v(-643.08, -925.51) * mm, "end": v(-641.31, -926.25) * mm});
            skPoint(sketch, "E125.visualSharp", {"position": v(-638.81, -926.25) * mm});
            skArc(sketch, "E125.filletArc", {"start": v(-641.31, -926.25) * mm, "mid": v(-639.55, -925.51) * mm, "end": v(-638.81, -923.75) * mm});
            skPoint(sketch, "E126.visualSharp", {"position": v(-383.81, -926.25) * mm});
            skArc(sketch, "E126.filletArc", {"start": v(-383.81, -923.75) * mm, "mid": v(-383.08, -925.51) * mm, "end": v(-381.31, -926.25) * mm});
            skPoint(sketch, "E127.visualSharp", {"position": v(-378.81, -926.25) * mm});
            skArc(sketch, "E127.filletArc", {"start": v(-381.31, -926.25) * mm, "mid": v(-379.55, -925.51) * mm, "end": v(-378.81, -923.75) * mm});
            skPoint(sketch, "E128.visualSharp", {"position": v(-643.81, -1261.25) * mm});
            skArc(sketch, "E128.filletArc", {"start": v(-641.31, -1261.25) * mm, "mid": v(-643.08, -1261.98) * mm, "end": v(-643.81, -1263.75) * mm});
            skPoint(sketch, "E129.visualSharp", {"position": v(-638.81, -1261.25) * mm});
            skArc(sketch, "E129.filletArc", {"start": v(-638.81, -1263.75) * mm, "mid": v(-639.55, -1261.98) * mm, "end": v(-641.31, -1261.25) * mm});
            skPoint(sketch, "E130.visualSharp", {"position": v(-383.81, -1261.25) * mm});
            skArc(sketch, "E130.filletArc", {"start": v(-381.31, -1261.25) * mm, "mid": v(-383.08, -1261.98) * mm, "end": v(-383.81, -1263.75) * mm});
            skPoint(sketch, "E131.visualSharp", {"position": v(-378.81, -1261.25) * mm});
            skArc(sketch, "E131.filletArc", {"start": v(-378.81, -1263.75) * mm, "mid": v(-379.55, -1261.98) * mm, "end": v(-381.31, -1261.25) * mm});
            skLineSegment(sketch, "E132.trimOffspring", {"start": v(-638.81, -903.75) * mm, "end": v(-383.81, -903.75) * mm});
            skLineSegment(sketch, "E133.trimOffspring", {"start": v(-378.81, -903.75) * mm, "end": v(-311.31, -903.75) * mm});
            skLineSegment(sketch, "E134.trimOffspring", {"start": v(-378.81, -1303.75) * mm, "end": v(-311.31, -1303.75) * mm});
            skLineSegment(sketch, "E135.trimOffspring", {"start": v(-638.81, -1303.75) * mm, "end": v(-383.81, -1303.75) * mm});
            skSolve(sketch);
        }
        {
            var Q0;
            Q0 = qSketchRegion(id + "F28", true);
            extrude(context, id + "F29", {"entities" : qUnion([Q0]), "depth" : 18 * mm, "offsetDistance" : 25 * mm});
        }
        {
            var Q0;
            Q0=qCreatedBy(makeId("Front.planeOp"),FACE);
            var sketch = newSketch(context, id + "F30", { "sketchPlane" : qUnion([Q0])});
            skLineSegment(sketch, "E136", {"start": v(0, -109.6) * mm, "end": v(95, -109.6) * mm});
            skLineSegment(sketch, "E137", {"start": v(95, -109.6) * mm, "end": v(95, -354.6) * mm});
            skLineSegment(sketch, "E138", {"start": v(95, -354.6) * mm, "end": v(100, -354.6) * mm});
            skLineSegment(sketch, "E139", {"start": v(100, -354.6) * mm, "end": v(100, -104.6) * mm});
            skLineSegment(sketch, "E140", {"start": v(100, -104.6) * mm, "end": v(0, -104.6) * mm});
            skLineSegment(sketch, "E141", {"start": v(0, -104.6) * mm, "end": v(0, -109.6) * mm});
            skSolve(sketch);
        }
        {
            var Q0;
            Q0 = qSketchRegion(id + "F30", true);
            extrude(context, id + "F31", {"entities" : qUnion([Q0]), "depth" : 40 * mm, "offsetDistance" : 25 * mm});
        }
        {
            var Q0;
            Q0=makeQuery(id+"F31.opExtrude","SWEPT_FACE",FACE,{"disambiguationData":[OSD([sQuery(id+"F30.wireOp",EDGE,"E139")])]});
            var sketch = newSketch(context, id + "F32", { "sketchPlane" : qUnion([Q0])});
            skLineSegment(sketch, "E142", {"start": v(-20, -354.6) * mm, "end": v(-20, -104.6) * mm, "construction": true});
            skLineSegment(sketch, "E143.bottom", {"start": v(-20, -344.6) * mm, "end": v(-20, -344.6) * mm});
            skLineSegment(sketch, "E143.top", {"start": v(-20, -294.6) * mm, "end": v(-20, -294.6) * mm});
            skLineSegment(sketch, "E143.left", {"start": v(-17.5, -342.1) * mm, "end": v(-17.5, -297.1) * mm});
            skLineSegment(sketch, "E143.right", {"start": v(-22.5, -342.1) * mm, "end": v(-22.5, -297.1) * mm});
            skPoint(sketch, "E144", {"position": v(-20, -294.6) * mm});
            skPoint(sketch, "E145.visualSharp", {"position": v(-22.5, -344.6) * mm});
            skArc(sketch, "E145.filletArc", {"start": v(-22.5, -342.1) * mm, "mid": v(-21.77, -343.87) * mm, "end": v(-20, -344.6) * mm});
            skPoint(sketch, "E146.visualSharp", {"position": v(-17.5, -344.6) * mm});
            skArc(sketch, "E146.filletArc", {"start": v(-20, -344.6) * mm, "mid": v(-18.23, -343.87) * mm, "end": v(-17.5, -342.1) * mm});
            skPoint(sketch, "E147.visualSharp", {"position": v(-17.5, -294.6) * mm});
            skArc(sketch, "E147.filletArc", {"start": v(-17.5, -297.1) * mm, "mid": v(-18.23, -295.34) * mm, "end": v(-20, -294.6) * mm});
            skPoint(sketch, "E148.visualSharp", {"position": v(-22.5, -294.6) * mm});
            skArc(sketch, "E148.filletArc", {"start": v(-20, -294.6) * mm, "mid": v(-21.77, -295.34) * mm, "end": v(-22.5, -297.1) * mm});
            skSolve(sketch);
        }
        {
            var Q0;
            Q0 = qSketchRegion(id + "F32", true);
            extrude(context, id + "F33", {"entities" : qUnion([Q0]), "operationType" : NewBodyOperationType.REMOVE, "endBound" : BoundingType.UP_TO_NEXT, "oppositeDirection" : true, "depth" : 25 * mm, "offsetDistance" : 25 * mm});
        }
        {
            var Q0;
            Q0=qCreatedBy(makeId("Front.planeOp"),FACE);
            var sketch = newSketch(context, id + "F34", { "sketchPlane" : qUnion([Q0])});
            skLineSegment(sketch, "E149", {"start": v(-354.21, -269.95) * mm, "end": v(-324.21, -269.95) * mm});
            skLineSegment(sketch, "E150", {"start": v(-324.21, -269.95) * mm, "end": v(-324.21, -219.95) * mm});
            skLineSegment(sketch, "E151", {"start": v(-324.21, -219.95) * mm, "end": v(-369.21, -219.95) * mm});
            skLineSegment(sketch, "E152", {"start": v(-369.21, -219.95) * mm, "end": v(-369.21, -214.95) * mm});
            skLineSegment(sketch, "E153", {"start": v(-369.21, -214.95) * mm, "end": v(-319.21, -214.95) * mm});
            skLineSegment(sketch, "E154", {"start": v(-319.21, -214.95) * mm, "end": v(-319.21, -274.95) * mm});
            skLineSegment(sketch, "E155", {"start": v(-319.21, -274.95) * mm, "end": v(-354.21, -274.95) * mm});
            skLineSegment(sketch, "E156", {"start": v(-354.21, -274.95) * mm, "end": v(-354.21, -269.95) * mm});
            skSolve(sketch);
        }
        {
            var Q0;
            Q0 = qSketchRegion(id + "F34", true);
            extrude(context, id + "F35", {"entities" : qUnion([Q0]), "depth" : 40 * mm, "offsetDistance" : 25 * mm});
        }
        {
            var Q0;
            Q0=makeQuery(id+"F35.opExtrude","SWEPT_FACE",FACE,{"disambiguationData":[OSD([sQuery(id+"F34.wireOp",EDGE,"E153")])]});
            var sketch = newSketch(context, id + "F36", { "sketchPlane" : qUnion([Q0])});
            skLineSegment(sketch, "E157", {"start": v(-369.21, -20) * mm, "end": v(-319.21, -20) * mm, "construction": true});
            skLineSegment(sketch, "E158.bottom", {"start": v(-336.71, -25) * mm, "end": v(-351.71, -25) * mm});
            skLineSegment(sketch, "E158.top", {"start": v(-336.71, -15) * mm, "end": v(-351.71, -15) * mm});
            skLineSegment(sketch, "E158.left", {"start": v(-331.71, -20) * mm, "end": v(-331.71, -20) * mm});
            skLineSegment(sketch, "E158.right", {"start": v(-356.71, -20) * mm, "end": v(-356.71, -20) * mm});
            skPoint(sketch, "E159", {"position": v(-356.71, -20) * mm});
            skPoint(sketch, "E160.visualSharp", {"position": v(-356.71, -15) * mm});
            skArc(sketch, "E160.filletArc", {"start": v(-351.71, -15) * mm, "mid": v(-355.25, -16.46) * mm, "end": v(-356.71, -20) * mm});
            skPoint(sketch, "E161.visualSharp", {"position": v(-356.71, -25) * mm});
            skArc(sketch, "E161.filletArc", {"start": v(-356.71, -20) * mm, "mid": v(-355.25, -23.54) * mm, "end": v(-351.71, -25) * mm});
            skPoint(sketch, "E162.visualSharp", {"position": v(-331.71, -25) * mm});
            skArc(sketch, "E162.filletArc", {"start": v(-336.71, -25) * mm, "mid": v(-333.18, -23.54) * mm, "end": v(-331.71, -20) * mm});
            skPoint(sketch, "E163.visualSharp", {"position": v(-331.71, -15) * mm});
            skArc(sketch, "E163.filletArc", {"start": v(-331.71, -20) * mm, "mid": v(-333.18, -16.46) * mm, "end": v(-336.71, -15) * mm});
            skSolve(sketch);
        }
        {
            var Q0;
            Q0 = qSketchRegion(id + "F36", true);
            extrude(context, id + "F37", {"entities" : qUnion([Q0]), "operationType" : NewBodyOperationType.REMOVE, "endBound" : BoundingType.UP_TO_NEXT, "oppositeDirection" : true, "depth" : 25 * mm, "offsetDistance" : 25 * mm});
        }
        {
            var Q0;
            Q0=makeQuery(id+"F29.opExtrude","SWEPT_FACE",FACE,{"disambiguationData":[OSD([sQuery(id+"F28.wireOp",EDGE,"E75.left")])]});
            var sketch = newSketch(context, id + "F38", { "sketchPlane" : qUnion([Q0])});
            skLineSegment(sketch, "E164.bottom", {"start": v(442.12, 18) * mm, "end": v(658.12, 18) * mm});
            skLineSegment(sketch, "E164.top", {"start": v(442.12, 0) * mm, "end": v(658.12, 0) * mm});
            skLineSegment(sketch, "E164.left", {"start": v(442.12, 18) * mm, "end": v(442.12, 0) * mm});
            skLineSegment(sketch, "E164.right", {"start": v(658.12, 18) * mm, "end": v(658.12, 0) * mm});
            skSolve(sketch);
        }
        {
            var Q0;
            Q0 = qSketchRegion(id + "F38", true);
            extrude(context, id + "F39", {"entities" : qUnion([Q0]), "operationType" : NewBodyOperationType.ADD, "depth" : 44 * mm, "offsetDistance" : 25 * mm});
        }
        {
            var Q0;
            Q0=qCreatedBy(makeId("Front.planeOp"),FACE);
            var sketch = newSketch(context, id + "F40", { "sketchPlane" : qUnion([Q0])});
            skLineSegment(sketch, "E165", {"start": v(268.8, -124.9) * mm, "end": v(317.8, -124.9) * mm});
            skLineSegment(sketch, "E166", {"start": v(317.8, -124.9) * mm, "end": v(317.8, -148.9) * mm});
            skLineSegment(sketch, "E167", {"start": v(317.8, -148.9) * mm, "end": v(268.8, -148.9) * mm});
            skLineSegment(sketch, "E168", {"start": v(268.8, -124.9) * mm, "end": v(215.4, -124.9) * mm, "construction": true});
            skArc(sketch, "E169", {"start": v(268.8, -124.9) * mm, "mid": v(280.8, -136.9) * mm, "end": v(268.8, -148.9) * mm});
            skSolve(sketch);
        }
        {
            var Q0;
            Q0 = qSketchRegion(id + "F40", true);
            var Q1;
            Q1=sQuery(id+"F40.wireOp",EDGE,"E166");
            revolve(context, id + "F41", {"surfaceOperationType" : NewSurfaceOperationType.NEW, "entities" : qUnion([Q0]), "axis" : qUnion([Q1]), "revolveType" : RevolveType.FULL});
        }
        {
            var Q0;
            Q0=qCreatedBy(makeId("Top.planeOp"),FACE);
            var sketch = newSketch(context, id + "F42", { "sketchPlane" : qUnion([Q0])});
            skLineSegment(sketch, "E170", {"start": v(350.8, -437.8) * mm, "end": v(370.73, -437.8) * mm});
            skLineSegment(sketch, "E171", {"start": v(372.46, -436.8) * mm, "end": v(403.7, -382.44) * mm});
            skLineSegment(sketch, "E172", {"start": v(405.43, -381.44) * mm, "end": v(425.77, -381.44) * mm});
            skLineSegment(sketch, "E173", {"start": v(348.93, -440.52) * mm, "end": v(352.78, -450.52) * mm});
            skLineSegment(sketch, "E174", {"start": v(354.64, -451.8) * mm, "end": v(425.77, -451.8) * mm});
            skLineSegment(sketch, "E175", {"start": v(425.77, -451.8) * mm, "end": v(425.77, -381.44) * mm, "construction": true});
            skPoint(sketch, "E176.visualSharp", {"position": v(353.27, -451.8) * mm});
            skArc(sketch, "E176.filletArc", {"start": v(352.78, -450.52) * mm, "mid": v(353.51, -451.45) * mm, "end": v(354.64, -451.8) * mm});
            skPoint(sketch, "E177.visualSharp", {"position": v(347.88, -437.8) * mm});
            skArc(sketch, "E177.filletArc", {"start": v(350.8, -437.8) * mm, "mid": v(349.15, -438.67) * mm, "end": v(348.93, -440.52) * mm});
            skPoint(sketch, "E178.visualSharp", {"position": v(371.88, -437.8) * mm});
            skArc(sketch, "E178.filletArc", {"start": v(370.73, -437.8) * mm, "mid": v(371.73, -437.53) * mm, "end": v(372.46, -436.8) * mm});
            skPoint(sketch, "E179.visualSharp", {"position": v(404.27, -381.44) * mm});
            skArc(sketch, "E179.filletArc", {"start": v(405.43, -381.44) * mm, "mid": v(404.43, -381.71) * mm, "end": v(403.7, -382.44) * mm});
            skArc(sketch, "E180.MirrorCS", {"start": v(498.76, -450.52) * mm, "mid": v(498.03, -451.45) * mm, "end": v(496.9, -451.8) * mm});
            skArc(sketch, "E181.MirrorCS", {"start": v(500.74, -437.8) * mm, "mid": v(502.4, -438.67) * mm, "end": v(502.6, -440.52) * mm});
            skArc(sketch, "E182.MirrorCS", {"start": v(446.11, -381.44) * mm, "mid": v(447.11, -381.71) * mm, "end": v(447.85, -382.44) * mm});
            skArc(sketch, "E183.MirrorCS", {"start": v(480.81, -437.8) * mm, "mid": v(479.81, -437.53) * mm, "end": v(479.08, -436.8) * mm});
            skLineSegment(sketch, "E184.MirrorCS", {"start": v(500.74, -437.8) * mm, "end": v(480.81, -437.8) * mm});
            skPoint(sketch, "E185.MirrorP", {"position": v(447.27, -381.44) * mm});
            skLineSegment(sketch, "E186.MirrorCS", {"start": v(479.08, -436.8) * mm, "end": v(447.85, -382.44) * mm});
            skLineSegment(sketch, "E187.MirrorCS", {"start": v(496.9, -451.8) * mm, "end": v(425.77, -451.8) * mm});
            skPoint(sketch, "E188.MirrorP", {"position": v(503.65, -437.8) * mm});
            skPoint(sketch, "E189.MirrorP", {"position": v(498.27, -451.8) * mm});
            skLineSegment(sketch, "E190.MirrorCS", {"start": v(502.6, -440.52) * mm, "end": v(498.76, -450.52) * mm});
            skPoint(sketch, "E191.MirrorP", {"position": v(479.65, -437.8) * mm});
            skLineSegment(sketch, "E192.MirrorCS", {"start": v(446.11, -381.44) * mm, "end": v(425.77, -381.44) * mm});
            skSolve(sketch);
        }
        {
            var Q0;
            Q0 = qSketchRegion(id + "F42", true);
            extrude(context, id + "F43", {"entities" : qUnion([Q0]), "depth" : 32 * mm, "offsetDistance" : 25 * mm});
        }
        {
            var Q0;
            Q0=makeQuery(id+"F43.opExtrude","SWEPT_FACE",FACE,{"disambiguationData":[OSD([sQuery(id+"F42.wireOp",EDGE,"E174"),sQuery(id+"F42.wireOp",EDGE,"E187.MirrorCS")])]});
            var Q1;
            Q1=makeQuery(id+"F43.opExtrude","SWEPT_FACE",FACE,{"disambiguationData":[OSD([sQuery(id+"F42.wireOp",EDGE,"E172"),sQuery(id+"F42.wireOp",EDGE,"E192.MirrorCS")])]});
            cPlane(context, id + "F44", {"entities" : qUnion([Q0, Q1]), "cplaneType" : CPlaneType.MID_PLANE, "offset" : 25 * mm, "width" : 150 * mm, "height" : 150 * mm});
        }
        {
            var Q0;
            Q0=makeQuery(id+"F43.opExtrude","CAP_EDGE",EDGE,{"disambiguationData":[OSD([sQuery(id+"F42.wireOp",EDGE,"E172"),sQuery(id+"F42.wireOp",EDGE,"E192.MirrorCS")])],"isStart":false});
            cPlane(context, id + "F45", {"entities" : qUnion([Q0]), "cplaneType" : CPlaneType.MID_PLANE, "offset" : 25 * mm, "width" : 150 * mm, "height" : 150 * mm});
        }
        {
            var Q0;
            Q0=makeQuery(id+"F43.opExtrude","CAP_FACE",FACE,{"disambiguationData":[OSD([sQuery(id+"F42.wireOp",EDGE,"E170"),sQuery(id+"F42.wireOp",EDGE,"E171"),sQuery(id+"F42.wireOp",EDGE,"E172"),sQuery(id+"F42.wireOp",EDGE,"E173"),sQuery(id+"F42.wireOp",EDGE,"E174"),sQuery(id+"F42.wireOp",EDGE,"E176.filletArc"),sQuery(id+"F42.wireOp",EDGE,"E177.filletArc"),sQuery(id+"F42.wireOp",EDGE,"E178.filletArc"),sQuery(id+"F42.wireOp",EDGE,"E179.filletArc"),sQuery(id+"F42.wireOp",EDGE,"E180.MirrorCS"),sQuery(id+"F42.wireOp",EDGE,"E181.MirrorCS"),sQuery(id+"F42.wireOp",EDGE,"E182.MirrorCS"),sQuery(id+"F42.wireOp",EDGE,"E183.MirrorCS"),sQuery(id+"F42.wireOp",EDGE,"E184.MirrorCS"),sQuery(id+"F42.wireOp",EDGE,"E186.MirrorCS"),sQuery(id+"F42.wireOp",EDGE,"E187.MirrorCS"),sQuery(id+"F42.wireOp",EDGE,"E190.MirrorCS"),sQuery(id+"F42.wireOp",EDGE,"E192.MirrorCS")])],"isStart":false});
            var Q1;
            Q1=makeQuery(id+"F43.opExtrude","CAP_FACE",FACE,{"disambiguationData":[OSD([sQuery(id+"F42.wireOp",EDGE,"E170"),sQuery(id+"F42.wireOp",EDGE,"E171"),sQuery(id+"F42.wireOp",EDGE,"E172"),sQuery(id+"F42.wireOp",EDGE,"E173"),sQuery(id+"F42.wireOp",EDGE,"E174"),sQuery(id+"F42.wireOp",EDGE,"E176.filletArc"),sQuery(id+"F42.wireOp",EDGE,"E177.filletArc"),sQuery(id+"F42.wireOp",EDGE,"E178.filletArc"),sQuery(id+"F42.wireOp",EDGE,"E179.filletArc"),sQuery(id+"F42.wireOp",EDGE,"E180.MirrorCS"),sQuery(id+"F42.wireOp",EDGE,"E181.MirrorCS"),sQuery(id+"F42.wireOp",EDGE,"E182.MirrorCS"),sQuery(id+"F42.wireOp",EDGE,"E183.MirrorCS"),sQuery(id+"F42.wireOp",EDGE,"E184.MirrorCS"),sQuery(id+"F42.wireOp",EDGE,"E186.MirrorCS"),sQuery(id+"F42.wireOp",EDGE,"E187.MirrorCS"),sQuery(id+"F42.wireOp",EDGE,"E190.MirrorCS"),sQuery(id+"F42.wireOp",EDGE,"E192.MirrorCS")])],"isStart":true});
            cPlane(context, id + "F46", {"entities" : qUnion([Q0, Q1]), "cplaneType" : CPlaneType.MID_PLANE, "offset" : 25 * mm, "width" : 150 * mm, "height" : 150 * mm});
        }
        {
            var Q0;
            Q0=qCreatedBy(id+"F44.planeOp",FACE);
            var sketch = newSketch(context, id + "F47", { "sketchPlane" : qUnion([Q0])});
            skLineSegment(sketch, "E193", {"start": v(376.77, 28) * mm, "end": v(425.77, 28) * mm});
            skLineSegment(sketch, "E194", {"start": v(425.77, 28) * mm, "end": v(425.77, 4) * mm});
            skLineSegment(sketch, "E195", {"start": v(425.77, 4) * mm, "end": v(376.77, 4) * mm});
            skLineSegment(sketch, "E196", {"start": v(376.77, 28) * mm, "end": v(309.18, 28) * mm, "construction": true});
            skArc(sketch, "E197", {"start": v(376.77, 28) * mm, "mid": v(388.77, 16) * mm, "end": v(376.77, 4) * mm});
            skPoint(sketch, "E198", {"position": v(425.77, 16) * mm});
            skSolve(sketch);
        }
        {
            var Q0;
            Q0 = qSketchRegion(id + "F47", true);
            var Q1;
            Q1=sQuery(id+"F47.wireOp",EDGE,"E194");
            revolve(context, id + "F48", {"operationType" : NewBodyOperationType.ADD, "surfaceOperationType" : NewSurfaceOperationType.NEW, "entities" : qUnion([Q0]), "axis" : qUnion([Q1]), "revolveType" : RevolveType.FULL});
        }
        {
            var Q0;
            Q0=makeQuery(id+"F43.opExtrude","SWEPT_FACE",FACE,{"disambiguationData":[OSD([sQuery(id+"F42.wireOp",EDGE,"E170")])]});
            var sketch = newSketch(context, id + "F49", { "sketchPlane" : qUnion([Q0])});
            skCircle(sketch, "E199", {"center": v(-363.27, 16) * mm, "radius": 4 * mm});
            skCircle(sketch, "E200.MirrorC", {"center": v(-488.27, 16) * mm, "radius": 4 * mm});
            skSolve(sketch);
        }
        {
            var Q0;
            Q0 = qSketchRegion(id + "F49", true);
            extrude(context, id + "F50", {"entities" : qUnion([Q0]), "operationType" : NewBodyOperationType.REMOVE, "endBound" : BoundingType.UP_TO_NEXT, "oppositeDirection" : true, "depth" : 25 * mm, "offsetDistance" : 25 * mm});
        }
        {
            var Q0;
            {var subQ0=makeQuery(id+"F5.boolean.opBoolean","COPY",FACE,{"derivedFrom":makeQuery(id+"F5.opExtrude","SWEPT_FACE",FACE,{"disambiguationData":[OSD([sQuery(id+"F4.wireOp",EDGE,"E1.left")])]})});var subQ8=makeQuery(id+"F3.opExtrude","SWEPT_FACE",FACE,{"disambiguationData":[OSD([sQuery(id+"F2.wireOp",EDGE,"E0.bottom")])]});var subQ9=makeQuery(id+"F9.opExtrude","SWEPT_FACE",FACE,{"disambiguationData":[OSD([sQuery(id+"F8.wireOp",EDGE,"E3.bottom")])]});Q0=makeQuery(id+"F11.boolean.opBoolean","SPLIT",FACE,{"disambiguationData":[TD([subQ0])],"derivedFrom":makeQuery(id+"F9.boolean.opBoolean","COPY",FACE,{"disambiguationData":[TD([subQ8])],"derivedFrom":subQ9})});}
            var sketch = newSketch(context, id + "F51", { "sketchPlane" : qUnion([Q0])});
            skLineSegment(sketch, "E201.bottom", {"start": v(-605, 40) * mm, "end": v(-565, 40) * mm});
            skLineSegment(sketch, "E201.top", {"start": v(-605, 0) * mm, "end": v(-565, 0) * mm});
            skLineSegment(sketch, "E201.left", {"start": v(-605, 40) * mm, "end": v(-605, 0) * mm});
            skLineSegment(sketch, "E201.right", {"start": v(-565, 40) * mm, "end": v(-565, 0) * mm});
            skSolve(sketch);
        }
        {
            var Q0;
            Q0 = qSketchRegion(id + "F51", true);
            extrude(context, id + "F52", {"entities" : qUnion([Q0]), "operationType" : NewBodyOperationType.ADD, "endBound" : BoundingType.UP_TO_NEXT, "depth" : 25 * mm, "offsetDistance" : 25 * mm});
        }
        {
            var Q0;
            Q0=qCreatedBy(id+"F13.planeOp",FACE);
            var sketch = newSketch(context, id + "F53", { "sketchPlane" : qUnion([Q0])});
            skLineSegment(sketch, "E202", {"start": v(960.55, 470.37) * mm, "end": v(1290.55, 470.37) * mm});
            skLineSegment(sketch, "E203", {"start": v(1290.55, 470.37) * mm, "end": v(1290.55, 750.37) * mm});
            skLineSegment(sketch, "E204", {"start": v(1290.55, 750.37) * mm, "end": v(1310.55, 750.37) * mm});
            skLineSegment(sketch, "E205", {"start": v(1310.55, 750.37) * mm, "end": v(1310.55, 450.37) * mm});
            skLineSegment(sketch, "E206", {"start": v(1310.55, 450.37) * mm, "end": v(960.55, 450.37) * mm});
            skLineSegment(sketch, "E207", {"start": v(960.55, 450.37) * mm, "end": v(960.55, 470.37) * mm});
            skSolve(sketch);
        }
        {
            var Q0;
            Q0 = qSketchRegion(id + "F53", true);
            extrude(context, id + "F54", {"entities" : qUnion([Q0]), "depth" : 2000 * mm, "offsetDistance" : 25 * mm});
        }
        {
            var Q0;
            Q0=qCreatedBy(makeId("Top.planeOp"),FACE);
            var sketch = newSketch(context, id + "F55", { "sketchPlane" : qUnion([Q0])});
            skCircle(sketch, "E208", {"center": v(280.3, 450.5) * mm, "radius": 12.5 * mm});
            skSolve(sketch);
        }
        {
            var Q0;
            Q0 = qSketchRegion(id + "F55", true);
            extrude(context, id + "F56", {"entities" : qUnion([Q0]), "depth" : 36 * mm, "offsetDistance" : 25 * mm});
        }
        {
            var Q0;
            Q0=makeQuery(id+"F56.opExtrude","CAP_FACE",FACE,{"disambiguationData":[OSD([sQuery(id+"F55.wireOp",EDGE,"E208")])],"isStart":true});
            var sketch = newSketch(context, id + "F57", { "sketchPlane" : qUnion([Q0])});
            skCircle(sketch, "E209", {"center": v(280.3, -450.5) * mm, "radius": 5 * mm});
            skSolve(sketch);
        }
        {
            var Q0;
            Q0 = qSketchRegion(id + "F57", true);
            extrude(context, id + "F58", {"entities" : qUnion([Q0]), "operationType" : NewBodyOperationType.ADD, "depth" : 20 * mm, "offsetDistance" : 25 * mm});
        }
    });
